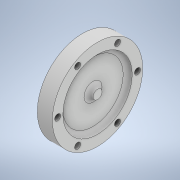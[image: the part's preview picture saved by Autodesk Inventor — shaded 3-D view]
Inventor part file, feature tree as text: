
AUTODESK INVENTOR PART (.ipt)
format: ipt  version: 2022 (Build 260153000, 153)  size: 161,280 bytes
history: native  units: mm
features: sketch x3, revolve x2, other x1, hole x1
ambient origin geometry x8: Origin, YZ Plane, XZ Plane, XY Plane, X Axis, Y Axis, Z Axis, Center Point
bodies: Body1 (feature_tree)
feature tree (7):
  other  "Твердое тело1"
  revolve  "Вращение1"
  revolve  "Вращение2"
  hole  "Отверстие1"  [1 undecoded]
  sketch  "Эскиз1"
  sketch  "Эскиз2"
  sketch  "Эскиз3"
note: 1 required parameter value undecoded (feature->parameter linkage not recoverable at this tier; creation-order binding heuristic only, values carry confidence <= 0.55)
